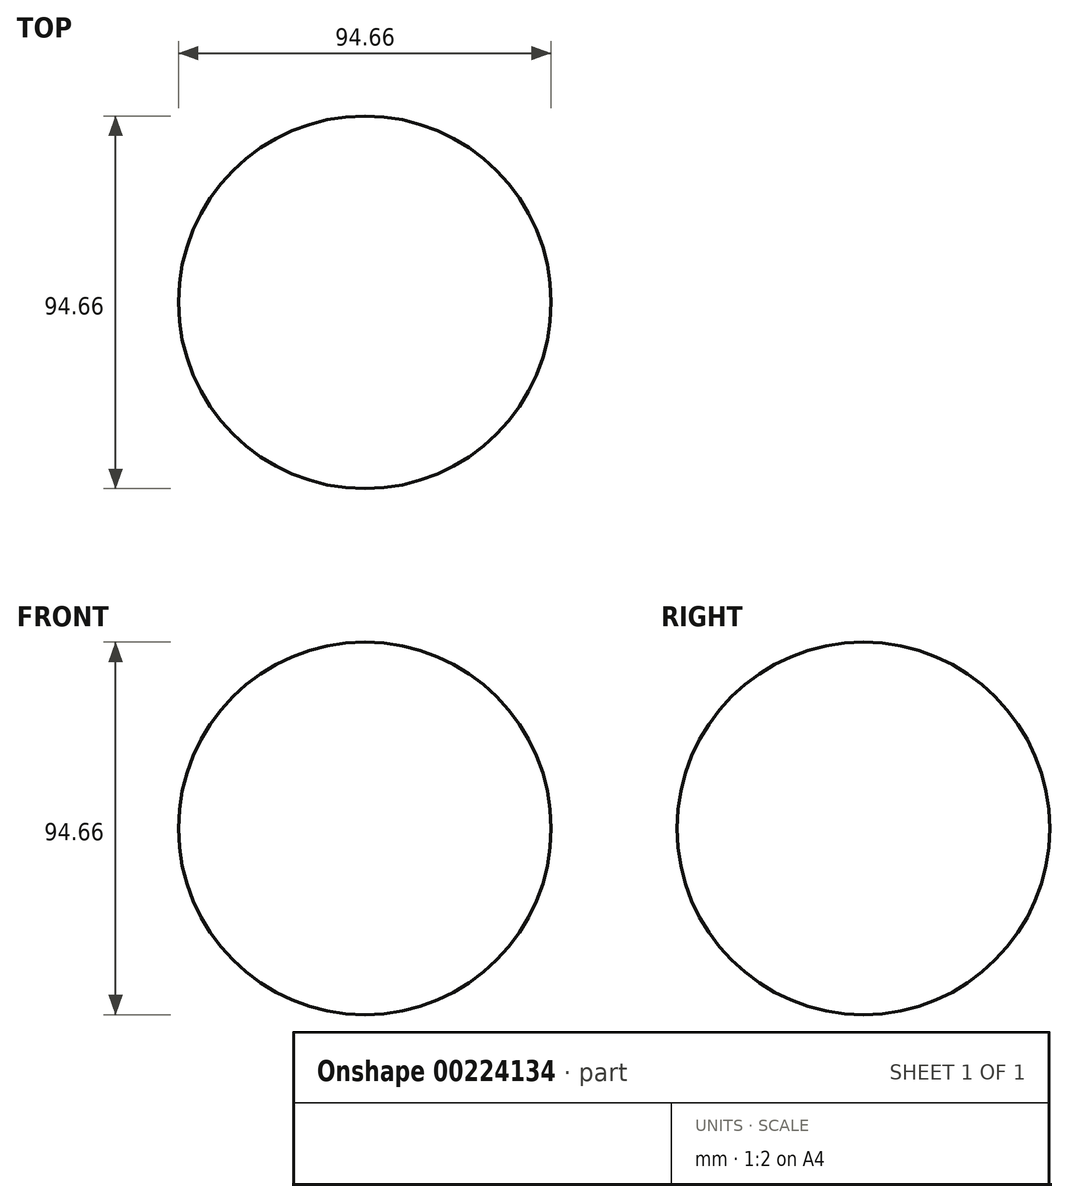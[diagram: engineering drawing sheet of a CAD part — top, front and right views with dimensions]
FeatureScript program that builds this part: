
annotation { "Feature Type Name" : "Feature", "Feature Type Description" : "" }
export const myFeature = defineFeature(function(context is Context, id is Id, definition is map)
    precondition{}
    {
        {
            var Q0;
            Q0=qCreatedBy(makeId("Front.planeOp"),FACE);
            var sketch = newSketch(context, id + "F0", { "sketchPlane" : qUnion([Q0])});
            skCircle(sketch, "E0", {"center": v(0, 0) * mm, "radius": 47.33 * mm});
            skLineSegment(sketch, "E1", {"start": v(0, 47.33) * mm, "end": v(0, -47.33) * mm});
            skSolve(sketch);
        }
        {
            var Q0;
            {var subQ0=sQuery(id+"F0.wireOp",EDGE,"E1");Q0=makeQuery(id+"F0.imprint","IMPRINT",FACE,{"disambiguationData":[TD([[makeQuery(id+"F0.imprint","IMPRINT",EDGE,{"derivedFrom":subQ0}),-1.0]])]});}
            var Q1;
            Q1=sQuery(id+"F0.wireOp",EDGE,"E1");
            revolve(context, id + "F1", {"entities" : qUnion([Q0]), "axis" : qUnion([Q1]), "revolveType" : RevolveType.FULL});
        }
    });
